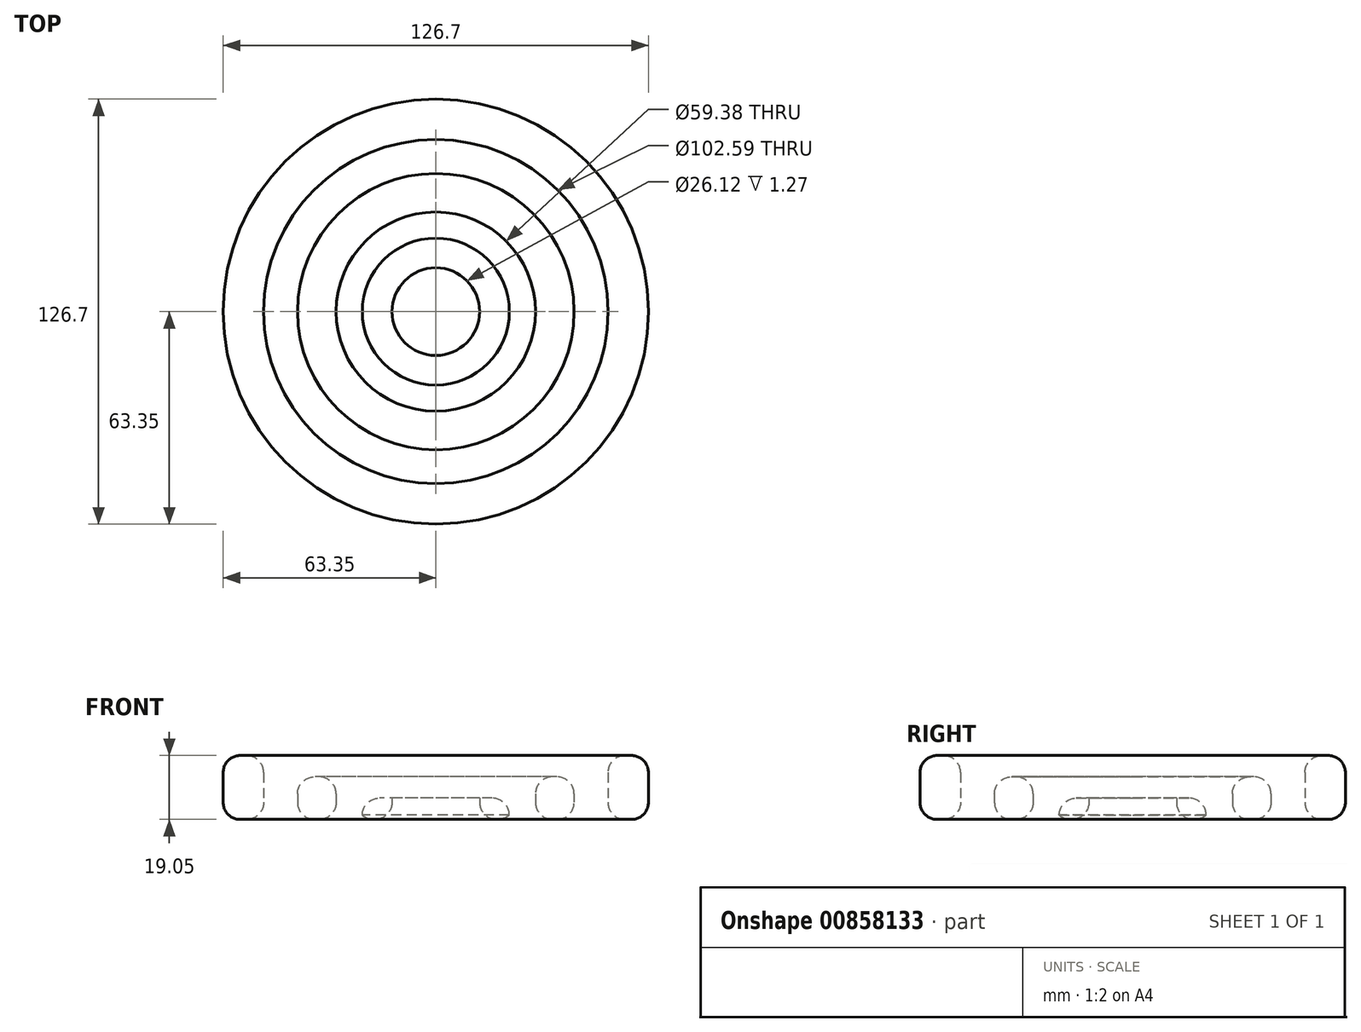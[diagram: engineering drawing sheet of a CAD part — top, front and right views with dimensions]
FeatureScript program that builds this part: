
annotation { "Feature Type Name" : "Feature", "Feature Type Description" : "" }
export const myFeature = defineFeature(function(context is Context, id is Id, definition is map)
    precondition{}
    {
        {
            var Q0;
            Q0=qCreatedBy(makeId("Top.planeOp"),FACE);
            var sketch = newSketch(context, id + "F0", { "sketchPlane" : qUnion([Q0])});
            skCircle(sketch, "E0", {"center": v(0, 0) * mm, "radius": 21.9 * mm});
            skCircle(sketch, "E1", {"center": v(0, 0) * mm, "radius": 13.06 * mm});
            skSolve(sketch);
        }
        {
            var Q0;
            Q0=makeQuery(id+"F0.imprint","IMPRINT",FACE,{"disambiguationData":[TD([[makeQuery(id+"F0.imprint","IMPRINT",EDGE,{"derivedFrom":sQuery(id+"F0.wireOp",EDGE,"E0")}),1.0]])]});
            extrude(context, id + "F1", {"entities" : qUnion([Q0]), "depth" : 6.35 * mm, "offsetDistance" : 25.4 * mm});
        }
        {
            var Q0;
            Q0=makeQuery(id+"F1.opExtrude","CAP_EDGE",EDGE,{"disambiguationData":[OSD([sQuery(id+"F0.wireOp",EDGE,"E0")])],"isStart":false});
            fillet(context, id + "F2", {"entities" : qUnion([Q0]), "radius" : 5.08 * mm, "tangentPropagation" : true, "allowEdgeOverflow" : false});
        }
        {
            var Q0;
            Q0=makeQuery(id+"F1.opExtrude","CAP_FACE",FACE,{"disambiguationData":[OSD([sQuery(id+"F0.wireOp",EDGE,"E0"),sQuery(id+"F0.wireOp",EDGE,"E1")])],"isStart":true});
            fillet(context, id + "F3", {"entities" : qUnion([Q0]), "radius" : 5.08 * mm, "tangentPropagation" : true, "allowEdgeOverflow" : false});
        }
        {
            var Q0;
            Q0=qCreatedBy(makeId("Top.planeOp"),FACE);
            var sketch = newSketch(context, id + "F4", { "sketchPlane" : qUnion([Q0])});
            skCircle(sketch, "E2", {"center": v(0, 0) * mm, "radius": 29.7 * mm});
            skCircle(sketch, "E3", {"center": v(0, 0) * mm, "radius": 41.2 * mm});
            skSolve(sketch);
        }
        {
            var Q0;
            Q0=makeQuery(id+"F4.imprint","IMPRINT",FACE,{"disambiguationData":[TD([[makeQuery(id+"F4.imprint","IMPRINT",EDGE,{"derivedFrom":sQuery(id+"F4.wireOp",EDGE,"E2")}),-1.0]])]});
            extrude(context, id + "F5", {"entities" : qUnion([Q0]), "depth" : 12.7 * mm, "offsetDistance" : 25.4 * mm});
        }
        {
            var Q0;
            Q0=makeQuery(id+"F5.opExtrude","CAP_EDGE",EDGE,{"disambiguationData":[OSD([sQuery(id+"F4.wireOp",EDGE,"E3")])],"isStart":true});
            fillet(context, id + "F6", {"entities" : qUnion([Q0]), "radius" : 5.08 * mm, "tangentPropagation" : true, "allowEdgeOverflow" : false});
        }
        {
            var Q0;
            Q0=makeQuery(id+"F5.opExtrude","CAP_EDGE",EDGE,{"disambiguationData":[OSD([sQuery(id+"F4.wireOp",EDGE,"E2")])],"isStart":true});
            fillet(context, id + "F7", {"entities" : qUnion([Q0]), "radius" : 5.08 * mm, "tangentPropagation" : true, "allowEdgeOverflow" : false});
        }
        {
            var Q0;
            Q0=makeQuery(id+"F5.opExtrude","CAP_FACE",FACE,{"disambiguationData":[OSD([sQuery(id+"F4.wireOp",EDGE,"E2"),sQuery(id+"F4.wireOp",EDGE,"E3")])],"isStart":false});
            fillet(context, id + "F8", {"entities" : qUnion([Q0]), "radius" : 5.08 * mm, "tangentPropagation" : true, "allowEdgeOverflow" : false});
        }
        {
            var Q0;
            Q0=qCreatedBy(makeId("Top.planeOp"),FACE);
            var sketch = newSketch(context, id + "F9", { "sketchPlane" : qUnion([Q0])});
            skCircle(sketch, "E4", {"center": v(0, 0) * mm, "radius": 51.3 * mm});
            skCircle(sketch, "E5", {"center": v(0, 0) * mm, "radius": 63.35 * mm});
            skSolve(sketch);
        }
        {
            var Q0;
            Q0=makeQuery(id+"F9.imprint","IMPRINT",FACE,{"disambiguationData":[TD([[makeQuery(id+"F9.imprint","IMPRINT",EDGE,{"derivedFrom":sQuery(id+"F9.wireOp",EDGE,"E4")}),-1.0]])]});
            extrude(context, id + "F10", {"entities" : qUnion([Q0]), "depth" : 19.05 * mm, "offsetDistance" : 25.4 * mm});
        }
        {
            var Q0;
            Q0=makeQuery(id+"F10.opExtrude","CAP_FACE",FACE,{"disambiguationData":[OSD([sQuery(id+"F9.wireOp",EDGE,"E4"),sQuery(id+"F9.wireOp",EDGE,"E5")])],"isStart":true});
            fillet(context, id + "F11", {"entities" : qUnion([Q0]), "radius" : 5.08 * mm, "tangentPropagation" : true, "allowEdgeOverflow" : false});
        }
        {
            var Q0;
            Q0=makeQuery(id+"F10.opExtrude","CAP_FACE",FACE,{"disambiguationData":[OSD([sQuery(id+"F9.wireOp",EDGE,"E4"),sQuery(id+"F9.wireOp",EDGE,"E5")])],"isStart":false});
            fillet(context, id + "F12", {"entities" : qUnion([Q0]), "radius" : 5.08 * mm, "tangentPropagation" : true, "allowEdgeOverflow" : false});
        }
    });
